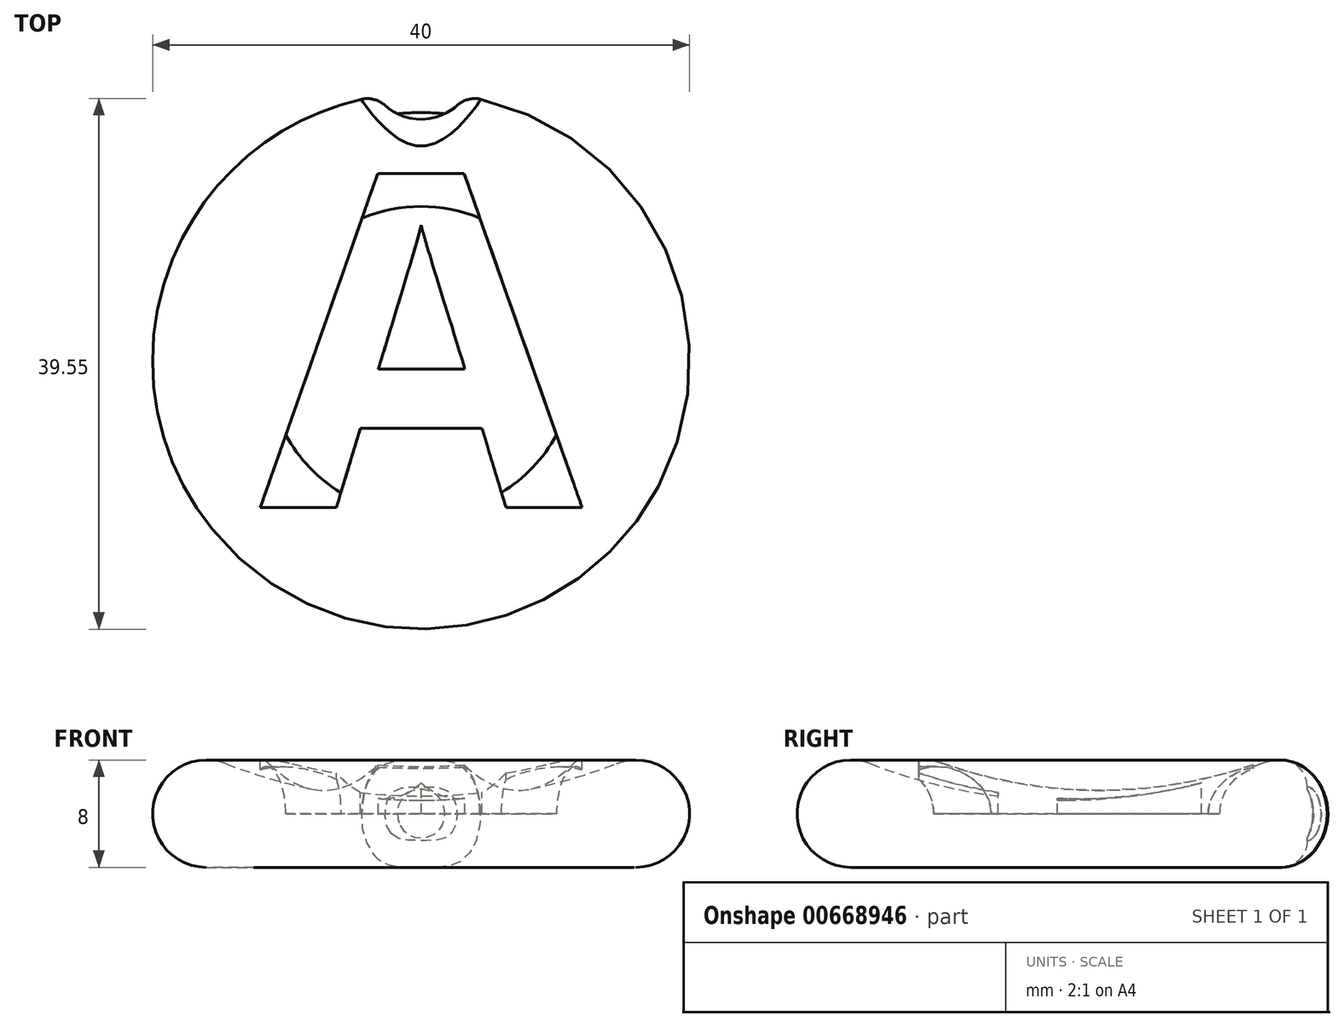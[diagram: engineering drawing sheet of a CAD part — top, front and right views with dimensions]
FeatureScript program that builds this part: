
annotation { "Feature Type Name" : "Feature", "Feature Type Description" : "" }
export const myFeature = defineFeature(function(context is Context, id is Id, definition is map)
    precondition{}
    {
        {
            var Q0;
            Q0=qCreatedBy(makeId("Front.planeOp"),FACE);
            var sketch = newSketch(context, id + "F0", { "sketchPlane" : qUnion([Q0])});
            skLineSegment(sketch, "E0", {"start": v(0, -29.5) * mm, "end": v(0, 39.42) * mm});
            skArc(sketch, "E1", {"start": v(-14.55, 7.73) * mm, "mid": v(-7.4, 5.69) * mm, "end": v(0, 5) * mm});
            skArc(sketch, "E2", {"start": v(-14.55, 7.73) * mm, "mid": v(-19.93, 4.74) * mm, "end": v(-16, 0) * mm});
            skLineSegment(sketch, "E3", {"start": v(0, 0) * mm, "end": v(-37.51, 0) * mm});
            skSolve(sketch);
        }
        {
            var Q0;
            {var subQ0=sQuery(id+"F0.wireOp",EDGE,"E1");Q0=makeQuery(id+"F0.imprint","IMPRINT",FACE,{"disambiguationData":[TD([[makeQuery(id+"F0.imprint","IMPRINT",EDGE,{"derivedFrom":subQ0}),-1.0]])]});}
            var Q1;
            Q1=sQuery(id+"F0.wireOp",EDGE,"E0");
            revolve(context, id + "F1", {"entities" : qUnion([Q0]), "axis" : qUnion([Q1]), "revolveType" : RevolveType.FULL});
        }
        {
            var Q0;
            Q0=qCreatedBy(makeId("Top.planeOp"),FACE);
            cPlane(context, id + "F2", {"entities" : qUnion([Q0]), "cplaneType" : CPlaneType.OFFSET, "offset" : 10 * mm, "width" : 150 * mm, "height" : 150 * mm});
        }
        {
            var Q0;
            Q0=qCreatedBy(id+"F2.planeOp",FACE);
            var sketch = newSketch(context, id + "F3", { "sketchPlane" : qUnion([Q0])});
            skText(sketch, "E4", { "text": "A", "fontName": "OpenSans-Bold.ttf"});
            const initialGuessF3  = {"E4": [-0.01197, -0.01092, 1, 0, 0.025]};
            skSetInitialGuess(sketch, initialGuessF3);
            skSolve(sketch);
        }
        {
            var Q0;
            Q0=makeQuery(id+"F3.imprint","IMPRINT",FACE,{"disambiguationData":[TD([[makeQuery(id+"F3.imprint","IMPRINT",EDGE,{"derivedFrom":sQuery(id+"F3.wireOp",EDGE,"E4.sketch_text.stroke-0")}),-1.0]])]});
            extrude(context, id + "F4", {"entities" : qUnion([Q0]), "operationType" : NewBodyOperationType.REMOVE, "oppositeDirection" : true, "depth" : 6 * mm, "offsetDistance" : 25 * mm});
        }
        {
            var Q0;
            Q0=qCreatedBy(id+"F2.planeOp",FACE);
            var sketch = newSketch(context, id + "F5", { "sketchPlane" : qUnion([Q0])});
            skCircle(sketch, "E5", {"center": v(0, 22) * mm, "radius": 4 * mm});
            skSolve(sketch);
        }
        {
            var Q0;
            Q0=makeQuery(id+"F5.imprint","IMPRINT",FACE,{"disambiguationData":[TD([[makeQuery(id+"F5.imprint","IMPRINT",EDGE,{"derivedFrom":sQuery(id+"F5.wireOp",EDGE,"E5")}),1.0]])]});
            extrude(context, id + "F6", {"entities" : qUnion([Q0]), "operationType" : NewBodyOperationType.REMOVE, "oppositeDirection" : true, "depth" : 25 * mm, "offsetDistance" : 25 * mm});
        }
        {
            var Q0;
            Q0=makeQuery(id+"F6.boolean.opBoolean","INTERSECT",EDGE,{"derivedFrom":[makeQuery(id+"F1.opRevolve","SWEPT_FACE",FACE,{"disambiguationData":[OSD([sQuery(id+"F0.wireOp",EDGE,"E2")])]}),makeQuery(id+"F6.opExtrude","SWEPT_FACE",FACE,{"disambiguationData":[OSD([sQuery(id+"F5.wireOp",EDGE,"E5")])]})]});
            fillet(context, id + "F7", {"entities" : qUnion([Q0]), "radius" : 2 * mm, "tangentPropagation" : true, "allowEdgeOverflow" : false});
        }
        {
            var Q0;
            Q0=qCreatedBy(makeId("Right.planeOp"),FACE);
            var sketch = newSketch(context, id + "F8", { "sketchPlane" : qUnion([Q0])});
            skLineSegment(sketch, "E6", {"start": v(0, 0) * mm, "end": v(0, 4) * mm});
            skLineSegment(sketch, "E7", {"start": v(0, 4) * mm, "end": v(15, 4) * mm});
            skCircle(sketch, "E8", {"center": v(15, 4) * mm, "radius": 3.5 * mm});
            skSolve(sketch);
        }
        {
            var Q0;
            Q0 = qSketchRegion(id + "F8", true);
            var Q1;
            Q1=sQuery(id+"F0.wireOp",EDGE,"E0");
            revolve(context, id + "F9", {"operationType" : NewBodyOperationType.ADD, "entities" : qUnion([Q0]), "axis" : qUnion([Q1]), "revolveType" : RevolveType.FULL});
        }
    });
